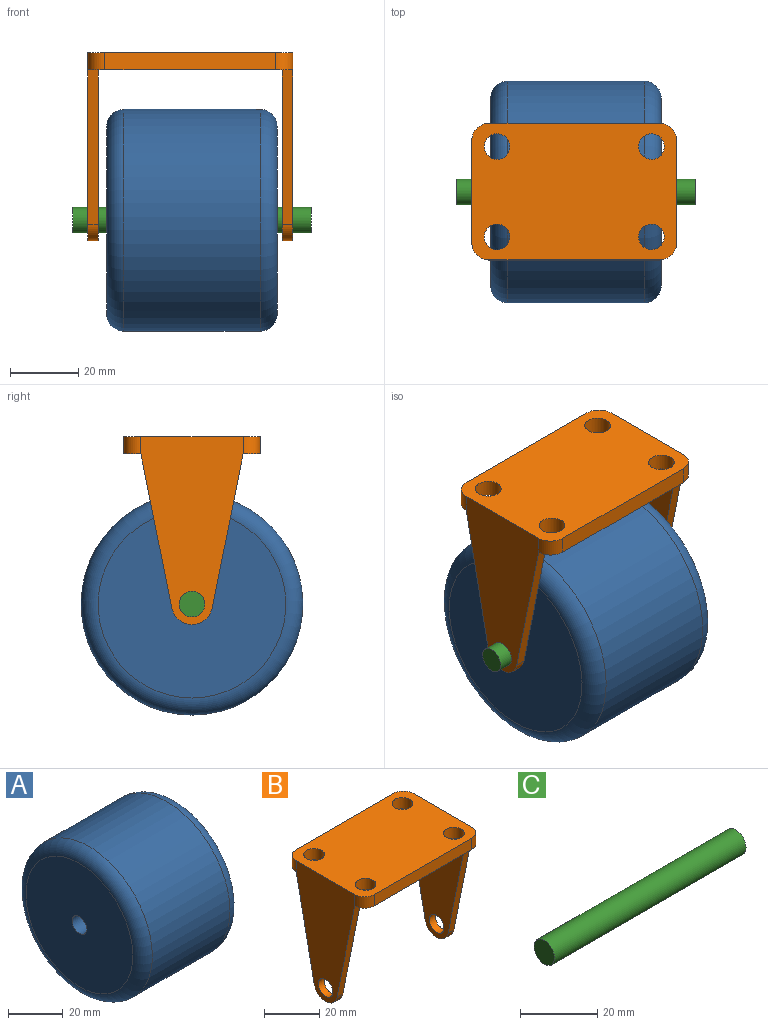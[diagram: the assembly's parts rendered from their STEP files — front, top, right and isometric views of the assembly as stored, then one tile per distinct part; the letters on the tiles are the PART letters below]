
ASSEMBLY  parts=3 mates=2
PART A: 6 faces, bbox 50x70.4x70.4 mm
  f0: cylinder r=3.75mm len=50mm, axis (-1,0,0), area 1178.1mm2, adj f2,f3
  f1: cylinder r=32.5mm len=65mm, axis (-1,0,0), area 8168.1mm2, adj f4,f5
  f2: plane 55x55mm, normal (1,0,0), area 2331.7mm2, adj f0,f5
  f3: plane 55x55mm, normal (-1,0,0), area 2331.7mm2, adj f0,f4
  f4: torus R=27.5mm, axis (1,0,0), area 1514.2mm2, adj f1,f3
  f5: torus R=27.5mm, axis (1,0,0), area 1514.2mm2, adj f1,f2
PART B: 24 faces, bbox 60x40x55 mm
  f0: plane 60x40mm, normal (0,0,-1), area 2021.8mm2, adj f1,f3,f4,f5,f6,f7,f10,f11
  f1: plane 50x5mm, normal (0,-1,0), area 250mm2, adj f0,f9,f10,f13
  f2: plane 55x30mm, normal (1,0,0), area 1091.8mm2, adj f9,f10,f11,f14,f15,f16,f17
  f3: plane 50x5mm, normal (0,1,0), area 250mm2, adj f0,f9,f11,f12
  f4: cylinder r=3.75mm len=7.5mm, axis (0,0,-1), area 117.8mm2, adj f0,f9
  f5: cylinder r=3.75mm len=7.5mm, axis (0,0,-1), area 117.8mm2, adj f0,f9
  f6: cylinder r=3.75mm len=7.5mm, axis (0,0,-1), area 117.8mm2, adj f0,f9
  f7: cylinder r=3.75mm len=7.5mm, axis (0,0,-1), area 117.8mm2, adj f0,f9
  f8: plane 55x30mm, normal (-1,0,0), area 1091.8mm2, adj f9,f12,f13,f19,f20,f21,f22
  f9: plane 60x40mm, normal (0,0,1), area 2201.8mm2, adj f1,f2,f3,f4,f5,f6,f7,f8
  f10: cylinder r=5mm len=5mm, axis (0,0,1), area 39.3mm2, adj f0,f1,f2,f9
  f11: cylinder r=5mm len=5mm, axis (0,0,-1), area 39.3mm2, adj f0,f2,f3,f9
  f12: cylinder r=5mm len=5mm, axis (0,0,1), area 39.3mm2, adj f0,f3,f8,f9
  f13: cylinder r=5mm len=5mm, axis (0,0,-1), area 39.3mm2, adj f0,f1,f8,f9
  f14: plane 45.19x9.12mm, normal (0,0.98,-0.2), area 138.3mm2, adj f0,f2,f17,f18
  f15: plane 45.19x9.12mm, normal (0,-0.98,-0.2), area 138.3mm2, adj f0,f2,f17,f18
  f16: cylinder r=3.75mm len=7.5mm, axis (1,0,0), area 70.7mm2, adj f2,f18
  f17: cylinder r=6mm len=11.76mm, axis (1,0,0), area 49.4mm2, adj f2,f14,f15,f18
  f18: plane 50x30mm, normal (-1,0,0), area 941.8mm2, adj f0,f14,f15,f16,f17
  f19: plane 45.19x9.12mm, normal (0,0.98,-0.2), area 138.3mm2, adj f0,f8,f22,f23
  f20: plane 45.19x9.12mm, normal (0,-0.98,-0.2), area 138.3mm2, adj f0,f8,f22,f23
  f21: cylinder r=3.75mm len=7.5mm, axis (-1,0,0), area 70.7mm2, adj f8,f23
  f22: cylinder r=6mm len=11.76mm, axis (-1,0,0), area 49.4mm2, adj f8,f19,f20,f23
  f23: plane 50x30mm, normal (1,0,0), area 941.8mm2, adj f0,f19,f20,f21,f22
PART C: 3 faces, bbox 70x7.5x7.5 mm
  f0: cylinder r=3.75mm len=70mm, axis (-1,0,0), area 1649.3mm2, adj f1,f2
  f1: plane 7.5x7.5mm, normal (1,0,0), area 44.2mm2, adj f0
  f2: plane 7.5x7.5mm, normal (-1,0,0), area 44.2mm2, adj f0
PLACE A t=(-23.62,-145.49,22.21)mm
PLACE B t=(0.9,-145.49,66.21)mm
PLACE C t=(-33.59,-145.49,22.21)mm
MATE cylindrical C.f0 <-> B.f16  axis (-1,0,0) through (-33.59,-145.49,22.21)mm
MATE cylindrical C.f0 <-> A.f0  axis (-1,0,0) through (1.41,-145.49,22.21)mm
